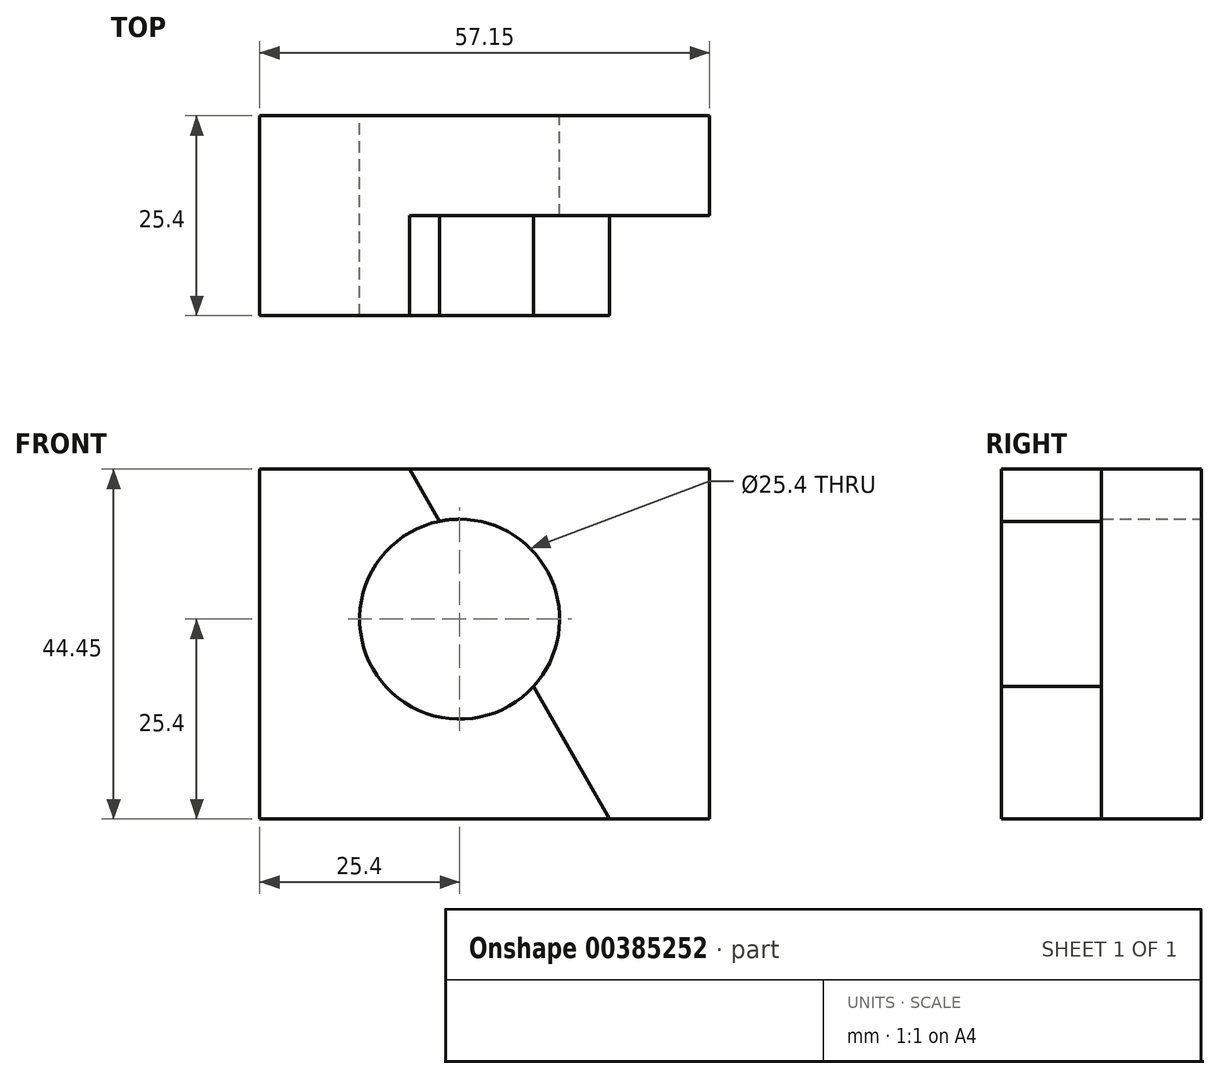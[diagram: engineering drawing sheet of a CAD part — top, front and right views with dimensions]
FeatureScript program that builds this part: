
annotation { "Feature Type Name" : "Feature", "Feature Type Description" : "" }
export const myFeature = defineFeature(function(context is Context, id is Id, definition is map)
    precondition{}
    {
        {
            var Q0;
            Q0=qCreatedBy(makeId("Front.planeOp"),FACE);
            var sketch = newSketch(context, id + "F0", { "sketchPlane" : qUnion([Q0])});
            skLineSegment(sketch, "E0", {"start": v(0, 0) * mm, "end": v(57.15, 0) * mm});
            skLineSegment(sketch, "E1", {"start": v(57.15, 0) * mm, "end": v(57.15, 44.45) * mm});
            skLineSegment(sketch, "E2", {"start": v(57.15, 44.45) * mm, "end": v(0, 44.45) * mm});
            skLineSegment(sketch, "E3", {"start": v(0, 44.45) * mm, "end": v(0, 0) * mm});
            skSolve(sketch);
        }
        {
            var Q0;
            Q0=qSketchRegion(id+"F0",true);
            extrude(context, id + "F1", {"entities" : qUnion([Q0]), "depth" : 25.4 * mm});
        }
        {
            var Q0;
            Q0=makeQuery(id+"F1.opExtrude","CAP_FACE",FACE,{"disambiguationData":[OSD([sQuery(id+"F0.wireOp",EDGE,"E0"),sQuery(id+"F0.wireOp",EDGE,"E1"),sQuery(id+"F0.wireOp",EDGE,"E2"),sQuery(id+"F0.wireOp",EDGE,"E3")])],"isStart":false});
            var sketch = newSketch(context, id + "F2", { "sketchPlane" : qUnion([Q0])});
            skLineSegment(sketch, "E4", {"start": v(19.05, 44.45) * mm, "end": v(44.45, 0) * mm});
            skSolve(sketch);
        }
        {
            var Q0;
            {var subQ0=sQuery(id+"F2.wireOp",EDGE,"E4");Q0=makeQuery(id+"F2.imprint","IMPRINT",FACE,{"disambiguationData":[TD([[makeQuery(id+"F2.imprint","IMPRINT",EDGE,{"derivedFrom":subQ0}),1.0]])]});}
            extrude(context, id + "F3", {"entities" : qUnion([Q0]), "operationType" : NewBodyOperationType.REMOVE, "oppositeDirection" : true, "depth" : 12.7 * mm});
        }
        {
            var Q0;
            Q0=makeQuery(id+"F1.opExtrude","CAP_FACE",FACE,{"disambiguationData":[OSD([sQuery(id+"F0.wireOp",EDGE,"E0"),sQuery(id+"F0.wireOp",EDGE,"E1"),sQuery(id+"F0.wireOp",EDGE,"E2"),sQuery(id+"F0.wireOp",EDGE,"E3")])],"isStart":true});
            var sketch = newSketch(context, id + "F4", { "sketchPlane" : qUnion([Q0])});
            skCircle(sketch, "E5", {"center": v(-25.4, 25.4) * mm, "radius": 12.7 * mm});
            skSolve(sketch);
        }
        {
            var Q0;
            Q0=makeQuery(id+"F4.imprint","IMPRINT",FACE,{"disambiguationData":[TD([[makeQuery(id+"F4.imprint","IMPRINT",EDGE,{"derivedFrom":sQuery(id+"F4.wireOp",EDGE,"E5")}),1.0]])]});
            extrude(context, id + "F5", {"entities" : qUnion([Q0]), "operationType" : NewBodyOperationType.REMOVE, "oppositeDirection" : true, "depth" : 25.4 * mm});
        }
    });
